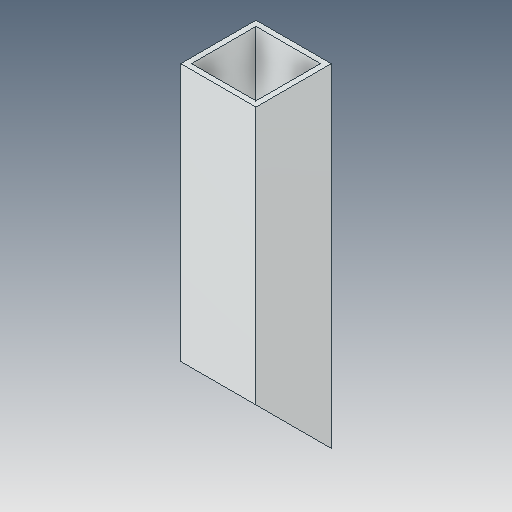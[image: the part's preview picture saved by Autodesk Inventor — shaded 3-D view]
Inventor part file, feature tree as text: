
AUTODESK INVENTOR PART (.ipt)
format: ipt  version: 2023.5 (Build 275446000, 446)  size: 89,600 bytes
history: native  units: in
note: dims shown in document units (in); Inventor stores cm internally (conversion verified against a paired STEP export)
features: chamfer x1
ambient origin geometry x8: Origin, YZ Plane, XZ Plane, XY Plane, X Axis, Y Axis, Z Axis, Center Point
bodies: Solid1 (feature_tree)
feature tree (1):
  chamfer  "Chamfer1"  [1 undecoded]
note: 1 required parameter value undecoded (feature->parameter linkage not recoverable at this tier; creation-order binding heuristic only, values carry confidence <= 0.55)
